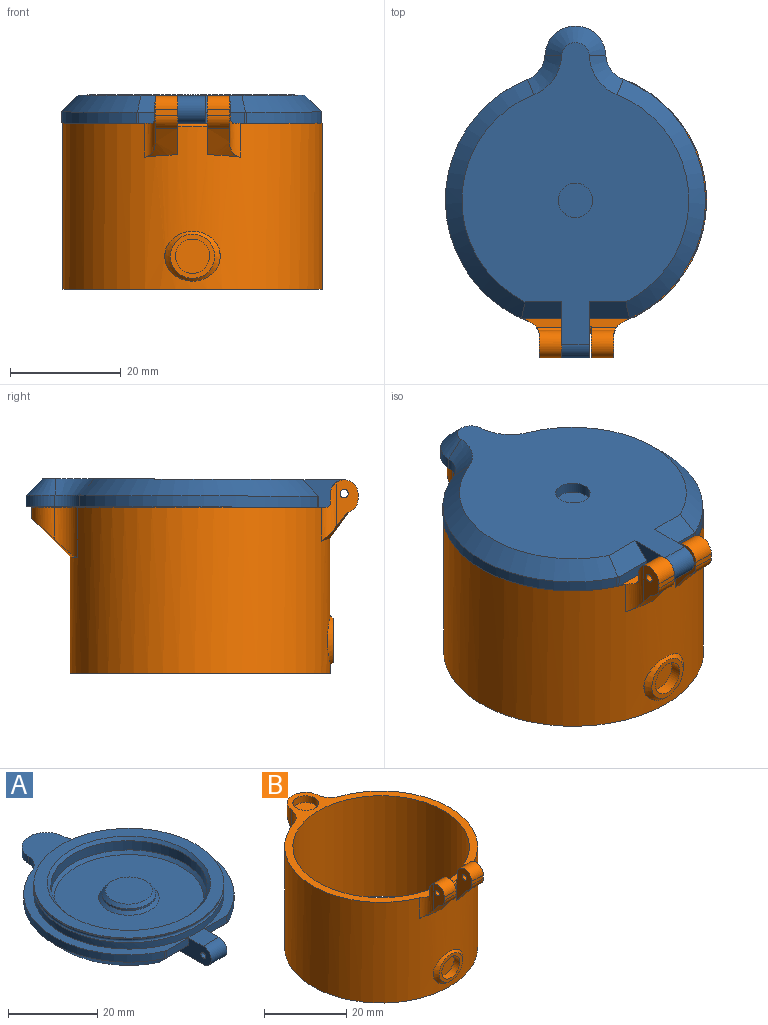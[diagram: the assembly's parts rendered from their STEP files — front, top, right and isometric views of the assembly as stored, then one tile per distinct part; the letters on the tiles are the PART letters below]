
ASSEMBLY  parts=2 mates=1
PART A: 36 faces, bbox 47x60x8 mm
  f0: cylinder r=6mm len=12mm, axis (0,0,1), area 18.8mm2, adj f6,f7
  f1: cylinder r=21.25mm len=42.5mm, axis (0,0,-1), area 33.4mm2, adj f2,f10
  f2: plane 42.5x42.5mm, normal (0,0,1), area 372.3mm2, adj f1,f9
  f3: cylinder r=17.5mm len=35mm, axis (0,0,1), area 274.9mm2, adj f8,f9
  f4: plane 33.5x33.5mm, normal (0,0,1), area 738.3mm2, adj f7,f8
  f5: plane 10.5x10.5mm, normal (0,0,1), area 86.6mm2, adj f6
  f6: cone r=5.25mm half-angle=45deg, axis (0,0,-1), area 37.5mm2, adj f0,f5
  f7: cone r=6mm half-angle=45deg, axis (0,0,-1), area 42.5mm2, adj f0,f4
  f8: cone r=16.75mm half-angle=45deg, axis (0,0,1), area 114.1mm2, adj f3,f4
  f9: cone r=17.5mm half-angle=45deg, axis (0,0,1), area 119.1mm2, adj f2,f3
  f10: torus R=21.57mm, axis (0,0,1), area 157.7mm2, adj f1,f35
  f11: plane 6.2x6.2mm, normal (0,0,-1), area 30.2mm2, adj f12
  f12: cylinder r=3.1mm len=6.2mm, axis (0,0,-1), area 39mm2, adj f11,f14
  f13: plane 7.31x3.03mm, normal (0,-0.71,-0.71), area 29.5mm2, adj f14,f21,f22,f23,f24
  f14: plane 54.5x41mm, normal (0,0,-1), area 1352.5mm2, adj f12,f13,f16,f17,f18,f19,f20,f21
  f15: cylinder r=0.75mm len=5mm, axis (1,0,0), area 23.6mm2, adj f24,f26
  f16: plane 7.31x3.03mm, normal (0,-0.71,-0.71), area 29.5mm2, adj f14,f17,f26,f27,f28
  f17: cone r=23.5mm half-angle=45deg, axis (0,0,1), area 216.6mm2, adj f14,f16,f18,f28,f29
  f18: cone r=8mm half-angle=45deg, axis (0,0,-1), area 31.6mm2, adj f14,f17,f19,f30
  f19: cone r=2.5mm half-angle=45deg, axis (0,0,1), area 51.7mm2, adj f14,f18,f20,f31
  f20: cone r=8mm half-angle=45deg, axis (0,0,-1), area 31.6mm2, adj f14,f19,f21,f32
  f21: cone r=23.5mm half-angle=45deg, axis (0,0,1), area 216.6mm2, adj f13,f14,f20,f22,f33
  f22: cylinder r=1mm len=2.02mm, axis (0,0,-1), area 0.9mm2, adj f13,f21,f23,f33,f34
  f23: plane 7.06x2mm, normal (0,-1,0), area 14.1mm2, adj f13,f22,f24,f34
  f24: plane 10.13x5mm, normal (1,0,0), area 35.7mm2, adj f13,f14,f15,f23,f25,f34
  f25: cylinder r=2.5mm len=5mm, axis (-1,0,0), area 39.3mm2, adj f14,f24,f26,f34
  f26: plane 10.13x5mm, normal (-1,0,0), area 35.7mm2, adj f14,f15,f16,f25,f27,f34
  f27: plane 7.06x2mm, normal (0,-1,0), area 14.1mm2, adj f16,f26,f28,f34
  f28: cylinder r=1mm len=2.02mm, axis (0,0,-1), area 0.9mm2, adj f16,f17,f27,f29,f34
  f29: cylinder r=23.5mm len=43.12mm, axis (0,0,-1), area 109.3mm2, adj f17,f28,f30,f34
  f30: cylinder r=5mm len=4.41mm, axis (0,0,-1), area 11.5mm2, adj f18,f29,f31,f34
  f31: cylinder r=5.5mm len=10.99mm, axis (0,0,1), area 33.5mm2, adj f19,f30,f32,f34
  f32: cylinder r=5mm len=4.41mm, axis (0,0,-1), area 11.5mm2, adj f20,f31,f33,f34
  f33: cylinder r=23.5mm len=43.12mm, axis (0,0,-1), area 109.3mm2, adj f21,f22,f32,f34
  f34: plane 57.5x47mm, normal (0,0,1), area 393.4mm2, adj f22,f23,f24,f25,f26,f27,f28,f29
  f35: cylinder r=21.25mm len=42.5mm, axis (0,0,-1), area 233mm2, adj f10,f34
PART B: 37 faces, bbox 47.4x59.4x35.4 mm
  f0: cylinder r=5mm len=2.65mm, axis (0,-1,0), area 0mm2, adj f1,f33
  f1: cylinder r=23.5mm len=47mm, axis (0,0,-1), area 4141.2mm2, adj f0,f2,f3,f11,f12,f13,f21,f22
  f2: cylinder r=5mm len=2.65mm, axis (0,-1,0), area 0mm2, adj f1,f33
  f3: bspline ~8.47x5.21mm, area 27.9mm2, adj f1,f4,f9,f11,f31
  f4: cylinder r=2.5mm len=4mm, axis (1,0,0), area 13mm2, adj f3,f5,f9,f11
  f5: plane 4x1mm, normal (0,-1,0), area 4mm2, adj f4,f6,f9,f11
  f6: cylinder r=2.5mm len=5mm, axis (-1,0,0), area 31.7mm2, adj f5,f7,f9,f11,f31
  f7: plane 4.23x1.9mm, normal (0,1,0), area 8mm2, adj f6,f8,f11,f31
  f8: plane 4.59x0.62mm, normal (0,0.71,0.71), area 3.7mm2, adj f7,f11,f27,f31
  f9: plane 8.45x3.96mm, normal (-1,0,0), area 20.6mm2, adj f3,f4,f5,f6,f10,f31
  f10: cylinder r=0.75mm len=4mm, axis (1,0,0), area 18.8mm2, adj f9,f11
  f11: plane 11.05x6.08mm, normal (1,0,0), area 32.4mm2, adj f1,f3,f4,f5,f6,f7,f8,f10
  f12: torus R=23mm, axis (0,0,1), area 4.3mm2, adj f1,f11,f13,f27
  f13: plane 11.05x6.08mm, normal (-1,0,0), area 32.4mm2, adj f1,f12,f14,f15,f16,f18,f19,f20
  f14: plane 4.59x0.62mm, normal (0,0.71,0.71), area 3.7mm2, adj f13,f15,f22,f27
  f15: plane 4.23x1.9mm, normal (0,1,0), area 8mm2, adj f13,f14,f16,f22
  f16: cylinder r=2.5mm len=5mm, axis (-1,0,0), area 31.7mm2, adj f13,f15,f17,f18,f22
  f17: plane 8.45x3.96mm, normal (1,0,0), area 20.6mm2, adj f16,f18,f19,f20,f21,f22
  f18: plane 4x1mm, normal (0,-1,0), area 4mm2, adj f13,f16,f17,f19
  f19: cylinder r=2.5mm len=4mm, axis (1,0,0), area 13mm2, adj f13,f17,f18,f21
  f20: cylinder r=0.75mm len=4mm, axis (1,0,0), area 18.8mm2, adj f13,f17
  f21: bspline ~8.47x5.21mm, area 27.9mm2, adj f1,f13,f17,f19,f22
  f22: cylinder r=3mm len=10.69mm, axis (0,0,-1), area 21.3mm2, adj f1,f14,f15,f16,f17,f21,f27
  f23: cylinder r=5mm len=9mm, axis (0,0,-1), area 41.9mm2, adj f1,f24,f25,f27
  f24: cylinder r=4.5mm len=8.96mm, axis (0,0,1), area 51.2mm2, adj f23,f25,f26,f27
  f25: cone r=30.5mm half-angle=45deg, axis (0,0,1), area 83.6mm2, adj f1,f23,f24,f26
  f26: cylinder r=5mm len=9mm, axis (0,0,-1), area 41.9mm2, adj f1,f24,f25,f27
  f27: plane 53.5x47mm, normal (0,0,1), area 310.6mm2, adj f1,f8,f11,f12,f13,f14,f22,f23
  f28: cylinder r=21.5mm len=43mm, axis (0,0,-1), area 4052.7mm2, adj f27,f32
  f29: cylinder r=3.1mm len=6.2mm, axis (0,0,1), area 39mm2, adj f27,f30
  f30: plane 6.2x6.2mm, normal (0,0,1), area 30.2mm2, adj f29
  f31: cylinder r=3mm len=10.69mm, axis (0,0,-1), area 21.3mm2, adj f1,f3,f6,f7,f8,f9,f27
  f32: plane 47x47mm, normal (0,0,-1), area 282.7mm2, adj f1,f28
  f33: cone r=4mm half-angle=45deg, axis (0,1,0), area 40mm2, adj f0,f1,f2,f34
  f34: plane 8x8mm, normal (0,-1,0), area 20.1mm2, adj f33,f35
  f35: cylinder r=3.1mm len=6.2mm, axis (0,-1,0), area 39mm2, adj f34,f36
  f36: plane 6.2x6.2mm, normal (0,-1,0), area 30.2mm2, adj f35
PLACE A rot(axis=(0,1,0),180deg) t=(-0.2,-0.01,35.11)mm
PLACE B at identity
MATE revolute B.f6 <-> A.f15  axis (1,0,0) through (-2.7,-26,32.5)mm
